# Revit family: Absperr- und Regulierklappe ZF-4219
name_source: partatom
category: Rohrzubehör
revit_build: Autodesk Revit 2018 (Build: 20190510_1515(x64)
units: mm (PartAtom-declared; Revit-internal decimal feet)

## family parameters
Arbeitsebenenbasiert = Nein
Beim Laden mit Abzugskörper schneiden = Nein
Bemaßung runder Anschluss = Durchmesser verwenden
Gemeinsam genutzt = Nein
Immer vertikal = Ja
Teiletyp = Unterbricht

## types (1)
- Absperr- und Regulierklappe ZF-4219
    Anschlussflansch = entsprechend EN1092-2
    Anwendungsgebiet = Geeignet für Flüssigkeiten in der Haustechnik, Kaltwasser, Heißwasser, etc.
    Gehäuse = GG, GJL-250/JL1040, entsprechend EN1561
    Gehäuseauskleidung = EPDM entsprechend ISO 1691
    Hebel DN 50-DN150 = Stahl, ST14.03
    Hebel DN200-300 = Stahl, S235 DIN2458/1626
    Hersteller = HERZ Armaturen Ges.m.b.H.
    Klappenscheibe = Edelstahl 1.4408
    Max. Betriebstemperatur = 110 °C
    Medium = Ethylen- und Propyleneglykol kann in einem Mischungsverhältnis zwischen 25 - 50 vol. [%] verwendet werden.
    Min. Betriebstemperatur = -20.00 °C bei entsprechender Wasser-Glycolmischung
    O-Ring = EPDM entsprechend ISO 1691
    PN = 16
    R_Dichtung = 2 mm  [stored 0.00656168 ft]
    SCRNCODE = 05;13;02
    SCRNSEQ = ARM;ARM_TYP="ALLF";2
    SCTWCODE = 04;07;02
    SCTWSEQ = FW;SBT_TYP_FW="101";2
    Spindel = Edelstahl ASTM-A276 / Type 316
    URL = www.herz-armaturen.at

note: [stored X ft] marks values corroborated as IEEE doubles in the binary element streams (Revit-internal decimal feet)
